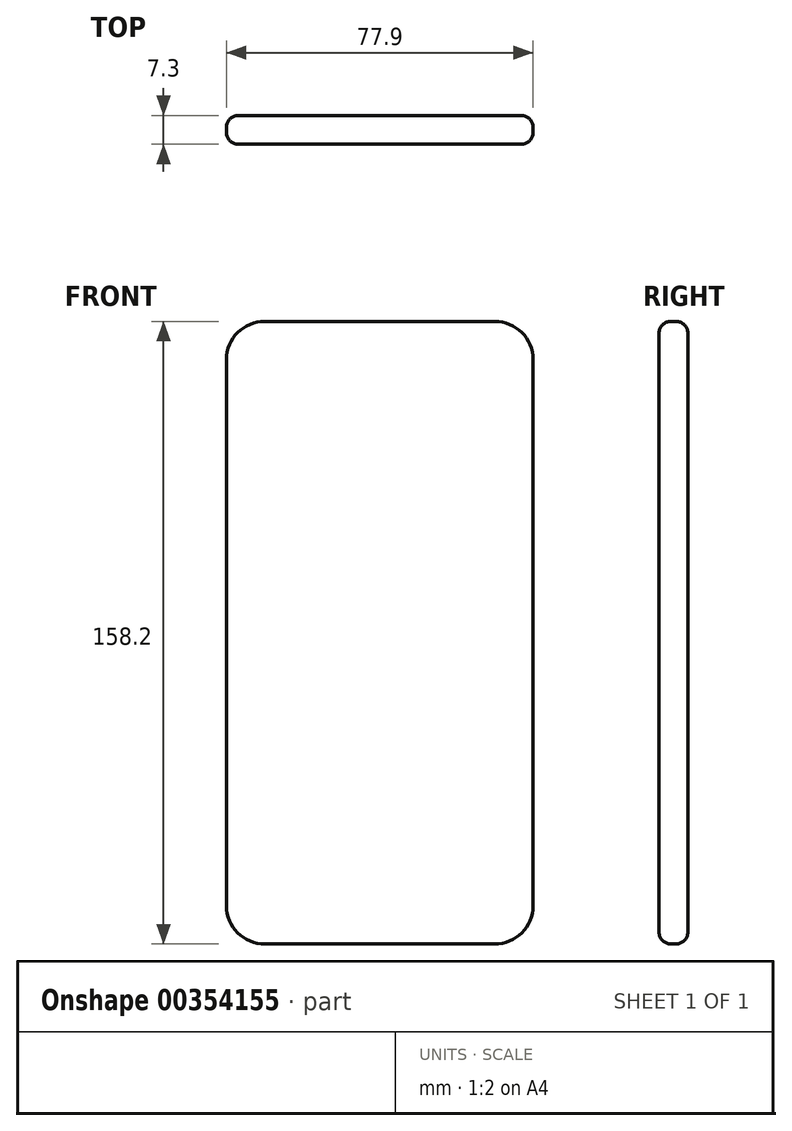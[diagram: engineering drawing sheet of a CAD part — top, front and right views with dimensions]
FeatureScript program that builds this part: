
annotation { "Feature Type Name" : "Feature", "Feature Type Description" : "" }
export const myFeature = defineFeature(function(context is Context, id is Id, definition is map)
    precondition{}
    {
        {
            var Q0;
            Q0=qCreatedBy(makeId("Front.planeOp"),FACE);
            var sketch = newSketch(context, id + "F0", { "sketchPlane" : qUnion([Q0])});
            skLineSegment(sketch, "E0.bottom", {"start": v(-29.23, 79.1) * mm, "end": v(29.23, 79.1) * mm});
            skLineSegment(sketch, "E0.top", {"start": v(-29.23, -79.1) * mm, "end": v(29.23, -79.1) * mm});
            skLineSegment(sketch, "E0.left", {"start": v(-38.95, 69.38) * mm, "end": v(-38.95, -69.38) * mm});
            skLineSegment(sketch, "E0.right", {"start": v(38.95, 69.38) * mm, "end": v(38.95, -69.38) * mm});
            skPoint(sketch, "E1.visualSharp", {"position": v(-38.95, 79.1) * mm});
            skArc(sketch, "E1.filletArc", {"start": v(-29.23, 79.1) * mm, "mid": v(-36.1, 76.25) * mm, "end": v(-38.95, 69.38) * mm});
            skPoint(sketch, "E2.visualSharp", {"position": v(38.95, 79.1) * mm});
            skArc(sketch, "E2.filletArc", {"start": v(38.95, 69.38) * mm, "mid": v(36.1, 76.25) * mm, "end": v(29.23, 79.1) * mm});
            skPoint(sketch, "E3.visualSharp", {"position": v(38.95, -79.1) * mm});
            skArc(sketch, "E3.filletArc", {"start": v(29.23, -79.1) * mm, "mid": v(36.1, -76.25) * mm, "end": v(38.95, -69.38) * mm});
            skPoint(sketch, "E4.visualSharp", {"position": v(-38.95, -79.1) * mm});
            skArc(sketch, "E4.filletArc", {"start": v(-38.95, -69.38) * mm, "mid": v(-36.1, -76.25) * mm, "end": v(-29.23, -79.1) * mm});
            skSolve(sketch);
        }
        {
            var Q0;
            Q0=makeQuery(id+"F0.imprint","IMPRINT",FACE,{"disambiguationData":[TD([[makeQuery(id+"F0.imprint","IMPRINT",EDGE,{"derivedFrom":sQuery(id+"F0.wireOp",EDGE,"E0.bottom")}),-1.0]])]});
            extrude(context, id + "F1", {"entities" : qUnion([Q0]), "depth" : 7.3 * mm});
        }
        {
            var Q0;
            Q0=makeQuery(id+"F1.opExtrude","CAP_FACE",FACE,{"disambiguationData":[OSD([sQuery(id+"F0.wireOp",EDGE,"E0.bottom"),sQuery(id+"F0.wireOp",EDGE,"E0.top"),sQuery(id+"F0.wireOp",EDGE,"E0.left"),sQuery(id+"F0.wireOp",EDGE,"E0.right"),sQuery(id+"F0.wireOp",EDGE,"E1.filletArc"),sQuery(id+"F0.wireOp",EDGE,"E2.filletArc"),sQuery(id+"F0.wireOp",EDGE,"E3.filletArc"),sQuery(id+"F0.wireOp",EDGE,"E4.filletArc")])],"isStart":false});
            var Q1;
            Q1=makeQuery(id+"F1.opExtrude","CAP_FACE",FACE,{"disambiguationData":[OSD([sQuery(id+"F0.wireOp",EDGE,"E0.bottom"),sQuery(id+"F0.wireOp",EDGE,"E0.top"),sQuery(id+"F0.wireOp",EDGE,"E0.left"),sQuery(id+"F0.wireOp",EDGE,"E0.right"),sQuery(id+"F0.wireOp",EDGE,"E1.filletArc"),sQuery(id+"F0.wireOp",EDGE,"E2.filletArc"),sQuery(id+"F0.wireOp",EDGE,"E3.filletArc"),sQuery(id+"F0.wireOp",EDGE,"E4.filletArc")])],"isStart":true});
            fillet(context, id + "F2", {"entities" : qUnion([Q0, Q1]), "radius" : 3 * mm, "tangentPropagation" : true, "allowEdgeOverflow" : false});
        }
    });
